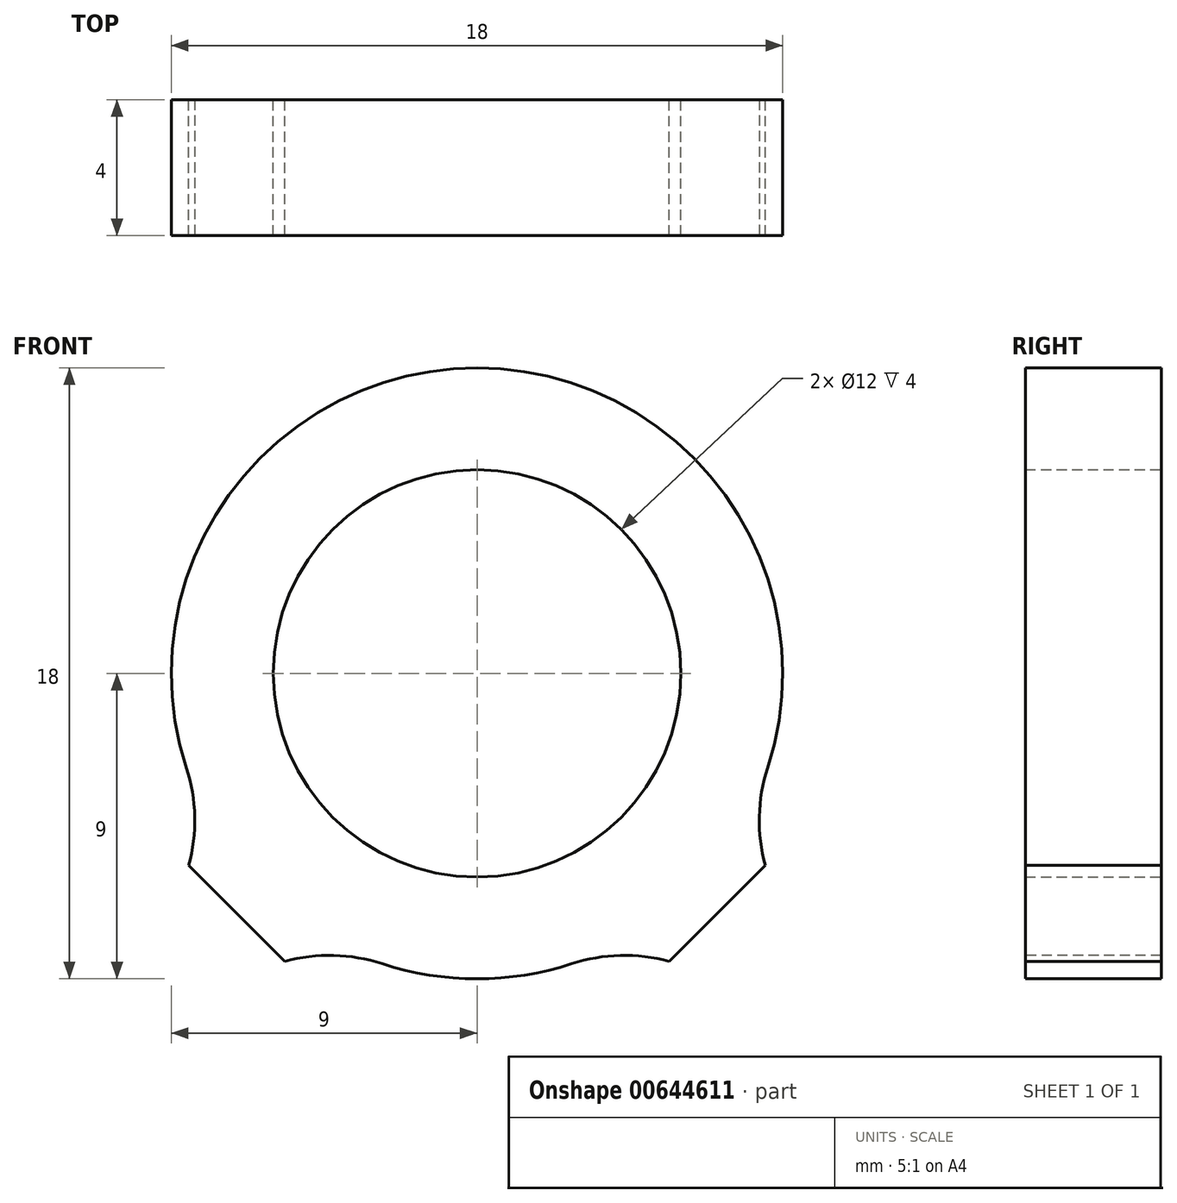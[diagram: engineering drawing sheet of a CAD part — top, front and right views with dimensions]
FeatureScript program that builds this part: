
annotation { "Feature Type Name" : "Feature", "Feature Type Description" : "" }
export const myFeature = defineFeature(function(context is Context, id is Id, definition is map)
    precondition{}
    {
        {
            var Q0;
            Q0=qCreatedBy(makeId("Front.planeOp"),FACE);
            var sketch = newSketch(context, id + "F0", { "sketchPlane" : qUnion([Q0])});
            skCircle(sketch, "E0", {"center": v(0, 0) * mm, "radius": 6 * mm});
            skLineSegment(sketch, "E1", {"start": v(0, 0) * mm, "end": v(7.07, -7.07) * mm, "construction": true});
            skArc(sketch, "E2.trimOffspring", {"start": v(-4.8, -7.62) * mm, "mid": v(0, -9) * mm, "end": v(4.8, -7.62) * mm});
            skLineSegment(sketch, "E3", {"start": v(8.49, -5.66) * mm, "end": v(5.66, -8.49) * mm});
            skArc(sketch, "E4.trimOffspring", {"start": v(7.62, -4.8) * mm, "mid": v(0, 9) * mm, "end": v(-7.62, -4.8) * mm});
            skLineSegment(sketch, "E5.trimOffspring", {"start": v(7.62, -4.8) * mm, "end": v(8.49, -5.66) * mm});
            skLineSegment(sketch, "E6.trimOffspring", {"start": v(4.8, -7.62) * mm, "end": v(5.66, -8.49) * mm});
            skLineSegment(sketch, "E7", {"start": v(0, 0) * mm, "end": v(0, -15.57) * mm});
            skLineSegment(sketch, "E8.MirrorCS", {"start": v(-7.62, -4.8) * mm, "end": v(-8.49, -5.66) * mm});
            skLineSegment(sketch, "E9.MirrorCS", {"start": v(-8.49, -5.66) * mm, "end": v(-5.66, -8.49) * mm});
            skLineSegment(sketch, "E10.MirrorCS", {"start": v(-4.8, -7.62) * mm, "end": v(-5.66, -8.49) * mm});
            skSolve(sketch);
        }
        {
            var Q0;
            Q0 = qSketchRegion(id + "F0", true);
            extrude(context, id + "F1", {"entities" : qUnion([Q0]), "endBound" : BoundingType.SYMMETRIC, "depth" : 4 * mm, "offsetDistance" : 25 * mm});
        }
        {
            var Q0;
            Q0=makeQuery(id+"F1.opExtrude","SWEPT_EDGE",EDGE,{"disambiguationData":[OSD([sQuery(id+"F0.wireOp",EDGE,"E4.trimOffspring"),sQuery(id+"F0.wireOp",EDGE,"E5.trimOffspring")])]});
            var Q1;
            Q1=makeQuery(id+"F1.opExtrude","SWEPT_EDGE",EDGE,{"disambiguationData":[OSD([sQuery(id+"F0.wireOp",EDGE,"E2.trimOffspring"),sQuery(id+"F0.wireOp",EDGE,"E6.trimOffspring")])]});
            var Q2;
            Q2=makeQuery(id+"F1.opExtrude","SWEPT_EDGE",EDGE,{"disambiguationData":[OSD([sQuery(id+"F0.wireOp",EDGE,"E2.trimOffspring"),sQuery(id+"F0.wireOp",EDGE,"E10.MirrorCS")])]});
            var Q3;
            Q3=makeQuery(id+"F1.opExtrude","SWEPT_EDGE",EDGE,{"disambiguationData":[OSD([sQuery(id+"F0.wireOp",EDGE,"E4.trimOffspring"),sQuery(id+"F0.wireOp",EDGE,"E8.MirrorCS")])]});
            fillet(context, id + "F2", {"entities" : qUnion([Q0, Q1, Q2, Q3]), "radius" : 5 * mm, "tangentPropagation" : true, "allowEdgeOverflow" : false});
        }
    });
